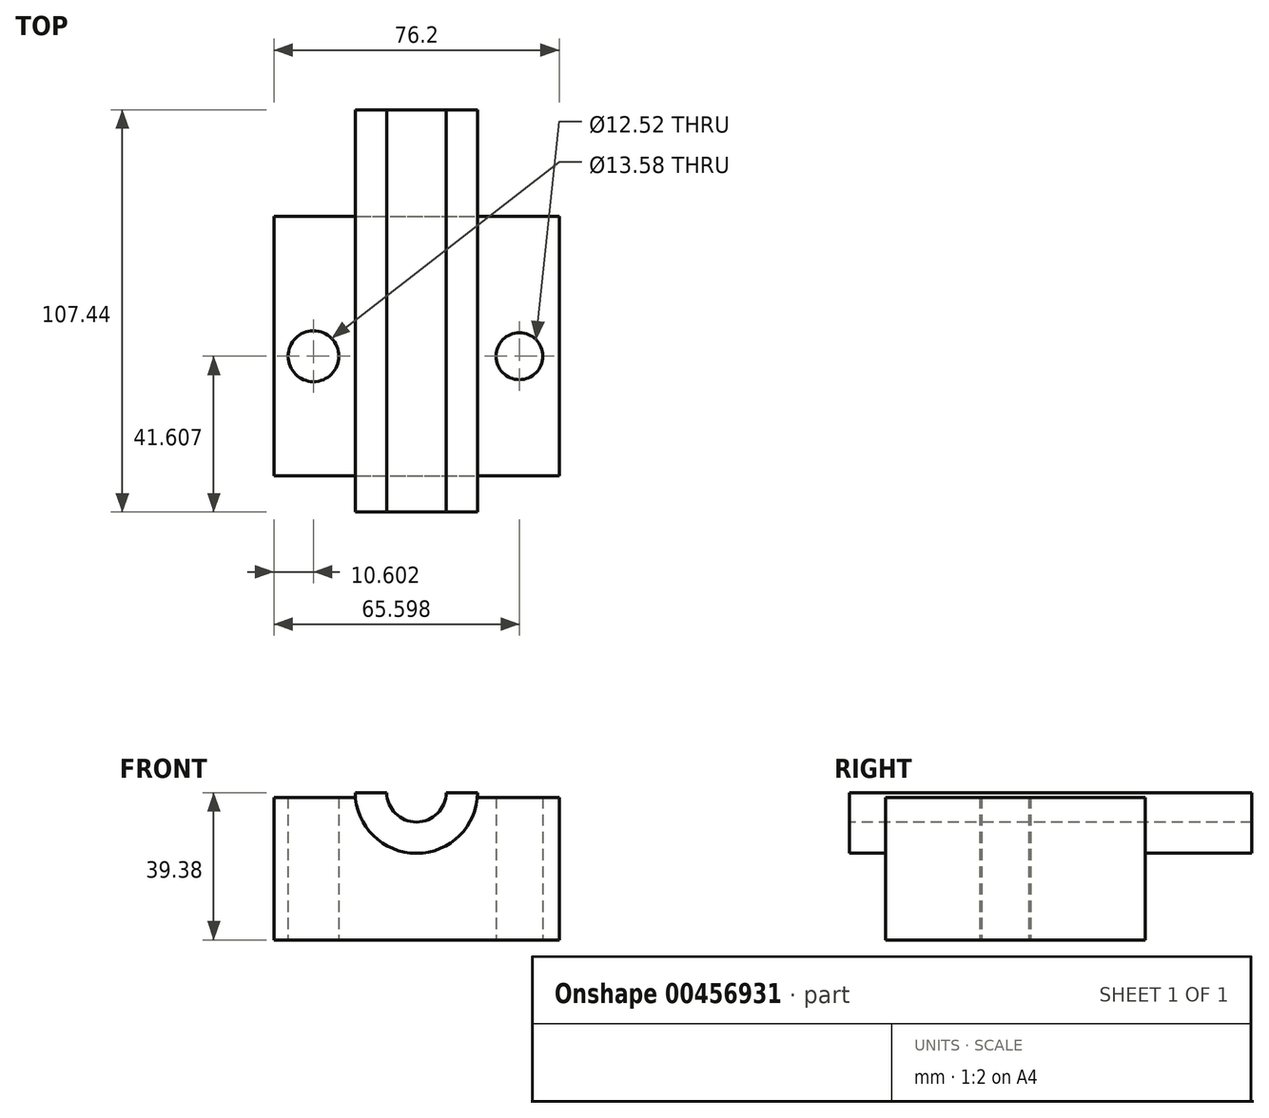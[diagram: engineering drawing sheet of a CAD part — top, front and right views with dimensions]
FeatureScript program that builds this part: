
annotation { "Feature Type Name" : "Feature", "Feature Type Description" : "" }
export const myFeature = defineFeature(function(context is Context, id is Id, definition is map)
    precondition{}
    {
        {
            var Q0;
            Q0=qCreatedBy(makeId("Front.planeOp"),FACE);
            var sketch = newSketch(context, id + "F0", { "sketchPlane" : qUnion([Q0])});
            skLineSegment(sketch, "E0.bottom", {"start": v(-38.1, 38.1) * mm, "end": v(0, 38.1) * mm});
            skLineSegment(sketch, "E0.top", {"start": v(-38.1, 0) * mm, "end": v(0, 0) * mm});
            skLineSegment(sketch, "E0.left", {"start": v(-38.1, 38.1) * mm, "end": v(-38.1, 0) * mm});
            skLineSegment(sketch, "E0.right", {"start": v(38.1, 38.1) * mm, "end": v(38.1, 0) * mm});
            skLineSegment(sketch, "E1", {"start": v(0, 38.1) * mm, "end": v(38.1, 38.1) * mm});
            skLineSegment(sketch, "E2", {"start": v(0, 0) * mm, "end": v(38.1, 0) * mm});
            skSolve(sketch);
        }
        {
            var Q0;
            Q0 = qSketchRegion(id + "F0", true);
            extrude(context, id + "F1", {"entities" : qUnion([Q0]), "depth" : 69.34 * mm});
        }
        {
            var Q0;
            Q0=qCreatedBy(makeId("Front.planeOp"),FACE);
            cPlane(context, id + "F2", {"entities" : qUnion([Q0]), "cplaneType" : CPlaneType.OFFSET, "offset" : 79 * mm, "width" : 152.4 * mm, "height" : 152.4 * mm});
        }
        {
            var Q0;
            Q0=qCreatedBy(id+"F2.planeOp",FACE);
            var sketch = newSketch(context, id + "F3", { "sketchPlane" : qUnion([Q0])});
            skArc(sketch, "E3", {"start": v(-16.35, 39.38) * mm, "mid": v(0, 23.15) * mm, "end": v(16.35, 39.38) * mm});
            skLineSegment(sketch, "E4", {"start": v(-16.35, 39.38) * mm, "end": v(16.35, 39.38) * mm});
            skSolve(sketch);
        }
        {
            var Q0;
            Q0=makeQuery(id+"F3.imprint","IMPRINT",FACE,{"disambiguationData":[TD([[makeQuery(id+"F3.imprint","IMPRINT",EDGE,{"derivedFrom":sQuery(id+"F3.wireOp",EDGE,"E3")}),1.0]])]});
            extrude(context, id + "F4", {"entities" : qUnion([Q0]), "operationType" : NewBodyOperationType.ADD, "oppositeDirection" : true, "depth" : 107.44 * mm, "offsetDistance" : 25.4 * mm});
        }
        {
            var Q0;
            Q0=qCreatedBy(id+"F2.planeOp",FACE);
            var sketch = newSketch(context, id + "F5", { "sketchPlane" : qUnion([Q0])});
            skArc(sketch, "E5", {"start": v(-7.97, 39.48) * mm, "mid": v(-0.03, 31.5) * mm, "end": v(7.97, 39.42) * mm});
            skLineSegment(sketch, "E6", {"start": v(-7.97, 39.48) * mm, "end": v(0, 39.48) * mm});
            skLineSegment(sketch, "E7", {"start": v(7.97, 39.42) * mm, "end": v(0, 39.48) * mm});
            skSolve(sketch);
        }
        {
            var Q0;
            Q0 = qSketchRegion(id + "F5", true);
            extrude(context, id + "F6", {"entities" : qUnion([Q0]), "operationType" : NewBodyOperationType.REMOVE, "oppositeDirection" : true, "depth" : 136.65 * mm});
        }
        {
            var Q0;
            Q0=qCreatedBy(makeId("Top.planeOp"),FACE);
            var sketch = newSketch(context, id + "F7", { "sketchPlane" : qUnion([Q0])});
            skCircle(sketch, "E8", {"center": v(-27.5, -37.38) * mm, "radius": 6.79 * mm});
            skCircle(sketch, "E9", {"center": v(27.5, -37.38) * mm, "radius": 6.26 * mm});
            skSolve(sketch);
        }
        {
            var Q0;
            Q0 = qSketchRegion(id + "F7", true);
            extrude(context, id + "F8", {"entities" : qUnion([Q0]), "operationType" : NewBodyOperationType.REMOVE, "depth" : 85.34 * mm});
        }
    });
